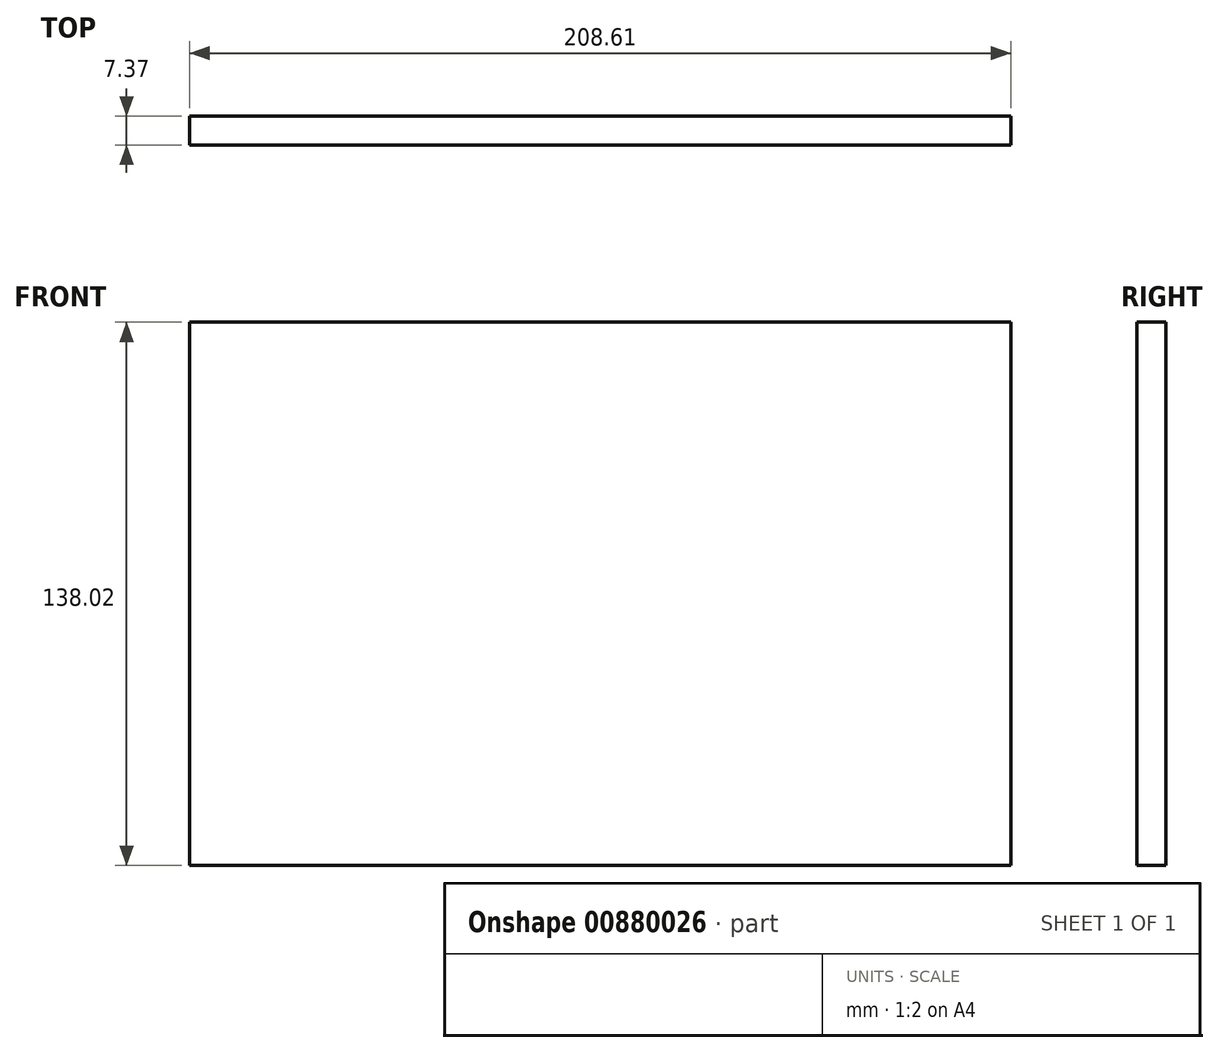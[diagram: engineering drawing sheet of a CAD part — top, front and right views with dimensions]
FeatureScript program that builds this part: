
annotation { "Feature Type Name" : "Feature", "Feature Type Description" : "" }
export const myFeature = defineFeature(function(context is Context, id is Id, definition is map)
    precondition{}
    {
        {
            var Q0;
            Q0=qCreatedBy(makeId("Front.planeOp"),FACE);
            var sketch = newSketch(context, id + "F0", { "sketchPlane" : qUnion([Q0])});
            skLineSegment(sketch, "E0", {"start": v(-81.19, 83.23) * mm, "end": v(101.8, 83.23) * mm});
            skLineSegment(sketch, "E1", {"start": v(101.8, 83.23) * mm, "end": v(101.8, -54.79) * mm});
            skLineSegment(sketch, "E2", {"start": v(101.8, -54.79) * mm, "end": v(-106.8, -54.79) * mm});
            skLineSegment(sketch, "E3", {"start": v(-106.8, -54.79) * mm, "end": v(-106.8, 83.23) * mm});
            skLineSegment(sketch, "E4", {"start": v(-106.8, 83.23) * mm, "end": v(-81.19, 83.23) * mm});
            skSolve(sketch);
        }
        {
            var Q0;
            Q0=makeQuery(id+"F0.imprint","IMPRINT",FACE,{"disambiguationData":[TD([[makeQuery(id+"F0.imprint","IMPRINT",EDGE,{"derivedFrom":sQuery(id+"F0.wireOp",EDGE,"E0")}),-1.0]])]});
            extrude(context, id + "F1", {"entities" : qUnion([Q0]), "depth" : 7.37 * mm, "offsetDistance" : 25.4 * mm});
        }
    });
